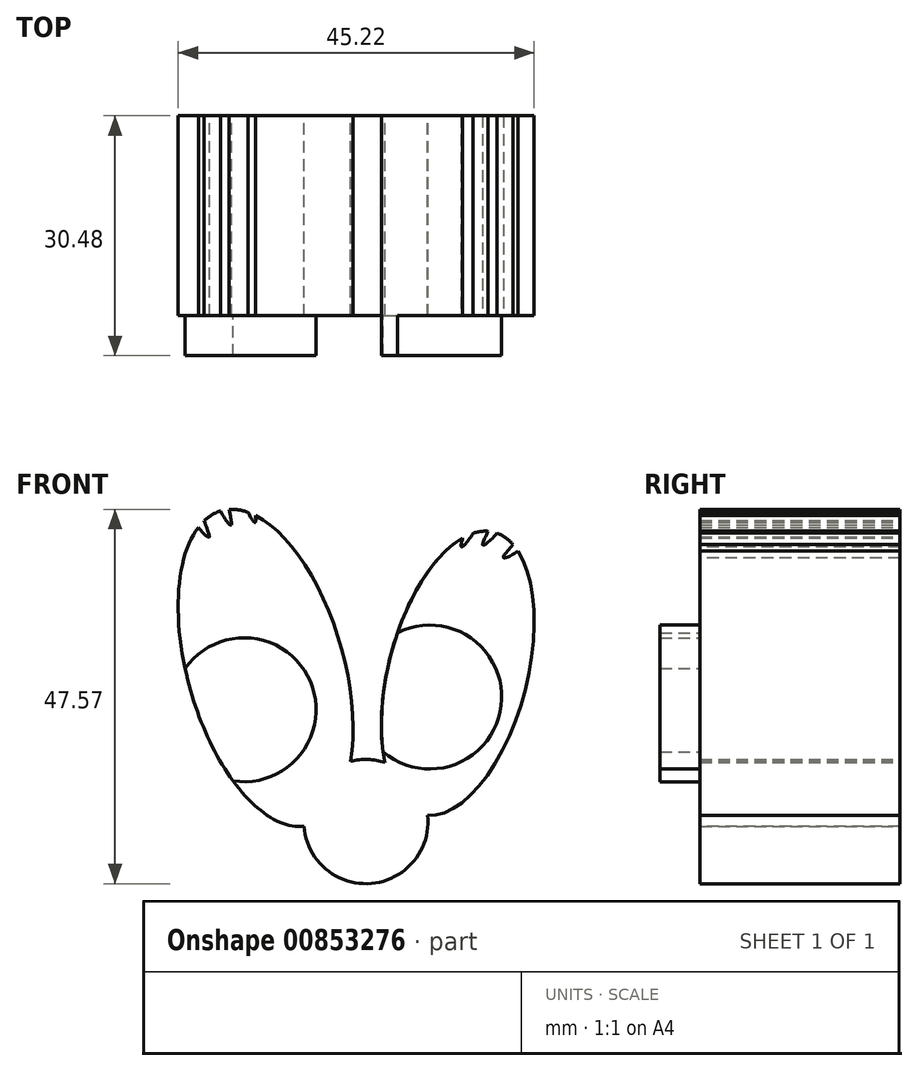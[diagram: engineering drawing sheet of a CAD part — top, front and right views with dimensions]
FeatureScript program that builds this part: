
annotation { "Feature Type Name" : "Feature", "Feature Type Description" : "" }
export const myFeature = defineFeature(function(context is Context, id is Id, definition is map)
    precondition{}
    {
        {
            var Q0;
            Q0=qCreatedBy(makeId("Front.planeOp"),FACE);
            var sketch = newSketch(context, id + "F0", { "sketchPlane" : qUnion([Q0])});
            skCircle(sketch, "E0", {"center": v(0, 0) * mm, "radius": 7.89 * mm});
            skEllipse(sketch, "E1", {"center": v(-12.74, 19.52) * mm, "majorRadius": 20.75 * mm, "minorRadius": 9.95 * mm, "majorAxis": v(-0.27, 0.96)});
            skEllipse(sketch, "E2", {"center": v(11.67, 18.84) * mm, "majorRadius": 18.5 * mm, "minorRadius": 8.82 * mm, "majorAxis": v(0.25, 0.97)});
            skFitSpline(sketch, "E3", {"points": [v(-19.93, 36.14) * mm, v(-22.67, 40.7) * mm, v(-20.85, 45.73) * mm, v(-21.15, 40.85) * mm, v(-19.93, 36.14) * mm]});
            skFitSpline(sketch, "E4", {"points": [v(-17.16, 37.65) * mm, v(-19.06, 42.62) * mm, v(-16.4, 47.25) * mm, v(-17.54, 42.5) * mm, v(-17.16, 37.65) * mm]});
            skFitSpline(sketch, "E5", {"points": [v(-14.08, 38.01) * mm, v(-15.55, 43.13) * mm, v(-12.48, 47.51) * mm, v(-14.04, 42.88) * mm, v(-14.08, 38.01) * mm]});
            skFitSpline(sketch, "E6", {"points": [v(39.7, 48.67) * mm, v(38.24, 53.8) * mm, v(41.3, 58.18) * mm, v(39.75, 53.55) * mm, v(39.7, 48.67) * mm]});
            skFitSpline(sketch, "E7.MirrorC", {"points": [v(17.47, 33.53) * mm, v(21.6, 36.88) * mm, v(21.61, 42.23) * mm, v(20.23, 37.54) * mm, v(17.47, 33.53) * mm]});
            skFitSpline(sketch, "E8.MirrorC", {"points": [v(14.87, 35.15) * mm, v(18, 39.47) * mm, v(16.62, 44.63) * mm, v(16.5, 39.75) * mm, v(14.87, 35.15) * mm]});
            skFitSpline(sketch, "E9.MirrorC", {"points": [v(12.14, 34.9) * mm, v(14.47, 39.69) * mm, v(12.21, 44.53) * mm, v(12.94, 39.7) * mm, v(12.14, 34.9) * mm]});
            skArc(sketch, "E10", {"start": v(-16.88, 5.18) * mm, "mid": v(-7.06, 17.8) * mm, "end": v(-22.97, 19.43) * mm});
            skArc(sketch, "E11", {"start": v(2.18, 8.87) * mm, "mid": v(17.18, 14.72) * mm, "end": v(4.02, 24) * mm});
            skSolve(sketch);
        }
        {
            var Q0;
            {var subQ0=sQuery(id+"F0.wireOp",EDGE,"E3");var subQ4=makeQuery(id+"F0.imprint","IMPRINT",VERTEX,{"derivedFrom":subQ0});Q0=makeQuery(id+"F0.imprint","IMPRINT",FACE,{"disambiguationData":[TD([[makeQuery(id+"F0.imprint","IMPRINT",EDGE,{"disambiguationData":[TD([[subQ4,1.0]])],"derivedFrom":subQ0}),-1.0]])]});}
            var Q1;
            {var subQ0=sQuery(id+"F0.wireOp",EDGE,"E4");var subQ4=makeQuery(id+"F0.imprint","IMPRINT",VERTEX,{"derivedFrom":subQ0});Q1=makeQuery(id+"F0.imprint","IMPRINT",FACE,{"disambiguationData":[TD([[makeQuery(id+"F0.imprint","IMPRINT",EDGE,{"disambiguationData":[TD([[subQ4,1.0]])],"derivedFrom":subQ0}),-1.0]])]});}
            var Q2;
            {var subQ0=sQuery(id+"F0.wireOp",EDGE,"E5");var subQ4=makeQuery(id+"F0.imprint","IMPRINT",VERTEX,{"derivedFrom":subQ0});Q2=makeQuery(id+"F0.imprint","IMPRINT",FACE,{"disambiguationData":[TD([[makeQuery(id+"F0.imprint","IMPRINT",EDGE,{"disambiguationData":[TD([[subQ4,1.0]])],"derivedFrom":subQ0}),-1.0]])]});}
            var Q3;
            {var subQ0=sQuery(id+"F0.wireOp",EDGE,"E2");var subQ1=sQuery(id+"F0.wireOp",EDGE,"E0");var subQ2=makeQuery(id+"F0.imprint","INTERSECT",VERTEX,{"disambiguationData":[OD(0.0)],"derivedFrom":[subQ1,subQ0]});Q3=makeQuery(id+"F0.imprint","IMPRINT",FACE,{"disambiguationData":[TD([[makeQuery(id+"F0.imprint","IMPRINT",EDGE,{"disambiguationData":[TD([[subQ2,-1.0]])],"derivedFrom":subQ1}),1.0]])]});}
            var Q4;
            {var subQ0=sQuery(id+"F0.wireOp",EDGE,"E9.MirrorC");var subQ4=makeQuery(id+"F0.imprint","IMPRINT",VERTEX,{"derivedFrom":subQ0});Q4=makeQuery(id+"F0.imprint","IMPRINT",FACE,{"disambiguationData":[TD([[makeQuery(id+"F0.imprint","IMPRINT",EDGE,{"disambiguationData":[TD([[subQ4,1.0]])],"derivedFrom":subQ0}),1.0]])]});}
            var Q5;
            {var subQ0=sQuery(id+"F0.wireOp",EDGE,"E8.MirrorC");var subQ4=makeQuery(id+"F0.imprint","IMPRINT",VERTEX,{"derivedFrom":subQ0});Q5=makeQuery(id+"F0.imprint","IMPRINT",FACE,{"disambiguationData":[TD([[makeQuery(id+"F0.imprint","IMPRINT",EDGE,{"disambiguationData":[TD([[subQ4,1.0]])],"derivedFrom":subQ0}),1.0]])]});}
            var Q6;
            {var subQ3=sQuery(id+"F0.wireOp",EDGE,"E11");Q6=makeQuery(id+"F0.imprint","IMPRINT",FACE,{"disambiguationData":[TD([[makeQuery(id+"F0.imprint","IMPRINT",EDGE,{"derivedFrom":subQ3}),-1.0]])]});}
            var Q7;
            {var subQ0=sQuery(id+"F0.wireOp",EDGE,"E10");Q7=makeQuery(id+"F0.imprint","IMPRINT",FACE,{"disambiguationData":[TD([[makeQuery(id+"F0.imprint","IMPRINT",EDGE,{"derivedFrom":subQ0}),1.0]])]});}
            var Q8;
            {var subQ3=sQuery(id+"F0.wireOp",EDGE,"E10");Q8=makeQuery(id+"F0.imprint","IMPRINT",FACE,{"disambiguationData":[TD([[makeQuery(id+"F0.imprint","IMPRINT",EDGE,{"derivedFrom":subQ3}),-1.0]])]});}
            var Q9;
            {var subQ0=sQuery(id+"F0.wireOp",EDGE,"E1");var subQ1=sQuery(id+"F0.wireOp",EDGE,"E0");var subQ2=makeQuery(id+"F0.imprint","INTERSECT",VERTEX,{"disambiguationData":[OD(0.0)],"derivedFrom":[subQ1,subQ0]});Q9=makeQuery(id+"F0.imprint","IMPRINT",FACE,{"disambiguationData":[TD([[makeQuery(id+"F0.imprint","IMPRINT",EDGE,{"disambiguationData":[TD([[subQ2,-1.0]])],"derivedFrom":subQ1}),1.0]])]});}
            var Q10;
            {var subQ0=sQuery(id+"F0.wireOp",EDGE,"E2");var subQ1=sQuery(id+"F0.wireOp",EDGE,"E0");var subQ2=makeQuery(id+"F0.imprint","INTERSECT",VERTEX,{"disambiguationData":[OD(0.0)],"derivedFrom":[subQ1,subQ0]});Q10=makeQuery(id+"F0.imprint","IMPRINT",FACE,{"disambiguationData":[TD([[makeQuery(id+"F0.imprint","IMPRINT",EDGE,{"disambiguationData":[TD([[subQ2,1.0]])],"derivedFrom":subQ1}),1.0]])]});}
            var Q11;
            {var subQ0=sQuery(id+"F0.wireOp",EDGE,"E11");Q11=makeQuery(id+"F0.imprint","IMPRINT",FACE,{"disambiguationData":[TD([[makeQuery(id+"F0.imprint","IMPRINT",EDGE,{"derivedFrom":subQ0}),1.0]])]});}
            var Q12;
            {var subQ0=sQuery(id+"F0.wireOp",EDGE,"E7.MirrorC");var subQ4=makeQuery(id+"F0.imprint","IMPRINT",VERTEX,{"derivedFrom":subQ0});Q12=makeQuery(id+"F0.imprint","IMPRINT",FACE,{"disambiguationData":[TD([[makeQuery(id+"F0.imprint","IMPRINT",EDGE,{"disambiguationData":[TD([[subQ4,1.0]])],"derivedFrom":subQ0}),1.0]])]});}
            var Q13;
            Q13=sQuery(id+"F0.wireOp",EDGE,"E4");
            var Q14;
            Q14=sQuery(id+"F0.wireOp",EDGE,"E1");
            var Q15;
            Q15=sQuery(id+"F0.wireOp",EDGE,"E2");
            var Q16;
            Q16=sQuery(id+"F0.wireOp",EDGE,"E10");
            var Q17;
            Q17=sQuery(id+"F0.wireOp",EDGE,"E11");
            var Q18;
            Q18=sQuery(id+"F0.wireOp",EDGE,"E3");
            var Q19;
            Q19=sQuery(id+"F0.wireOp",EDGE,"E5");
            var Q20;
            Q20=sQuery(id+"F0.wireOp",EDGE,"E7.MirrorC");
            var Q21;
            Q21=sQuery(id+"F0.wireOp",EDGE,"E8.MirrorC");
            var Q22;
            Q22=sQuery(id+"F0.wireOp",EDGE,"E0");
            var Q23;
            Q23=sQuery(id+"F0.wireOp",EDGE,"E9.MirrorC");
            extrude(context, id + "F1", {"entities" : qUnion([Q0, Q1, Q2, Q3, Q4, Q5, Q6, Q7, Q8, Q9, Q10, Q11, Q12]), "surfaceEntities" : qUnion([Q13, Q14, Q15, Q16, Q17, Q18, Q19, Q20, Q21, Q22, Q23]), "depth" : 25.4 * mm, "offsetDistance" : 25.4 * mm});
        }
        {
            var Q0;
            {var subQ0=sQuery(id+"F0.wireOp",EDGE,"E10");Q0=makeQuery(id+"F0.imprint","IMPRINT",FACE,{"disambiguationData":[TD([[makeQuery(id+"F0.imprint","IMPRINT",EDGE,{"derivedFrom":subQ0}),1.0]])]});}
            var Q1;
            {var subQ0=sQuery(id+"F0.wireOp",EDGE,"E11");Q1=makeQuery(id+"F0.imprint","IMPRINT",FACE,{"disambiguationData":[TD([[makeQuery(id+"F0.imprint","IMPRINT",EDGE,{"derivedFrom":subQ0}),1.0]])]});}
            extrude(context, id + "F2", {"entities" : qUnion([Q0, Q1]), "operationType" : NewBodyOperationType.ADD, "depth" : 30.48 * mm, "offsetDistance" : 25.4 * mm});
        }
    });
